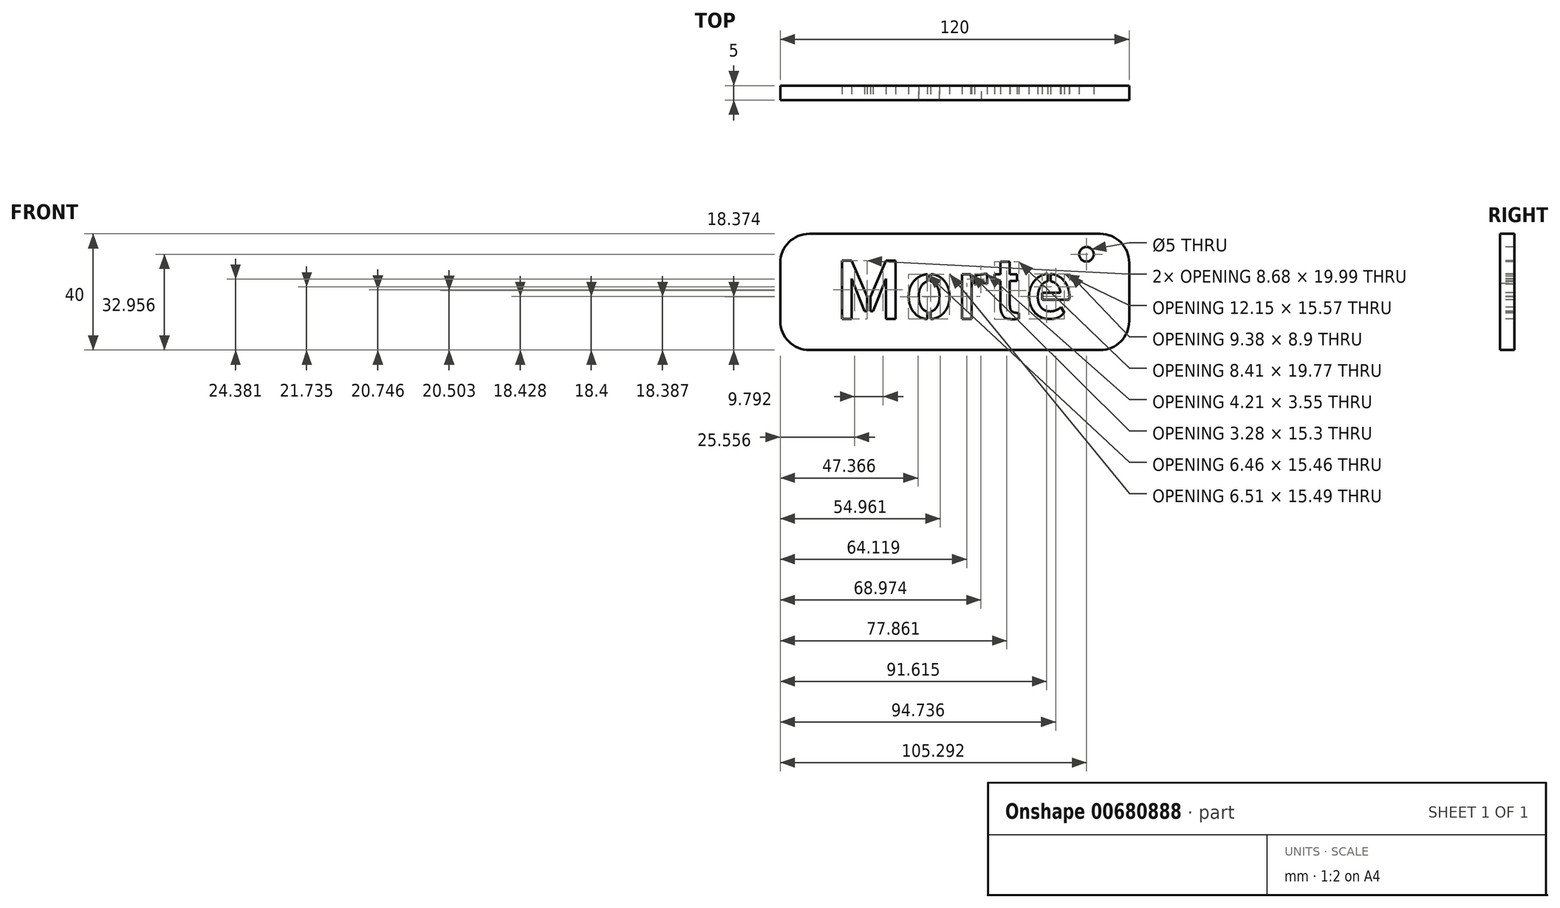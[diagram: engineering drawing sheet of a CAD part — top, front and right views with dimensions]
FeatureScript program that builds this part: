
annotation { "Feature Type Name" : "Feature", "Feature Type Description" : "" }
export const myFeature = defineFeature(function(context is Context, id is Id, definition is map)
    precondition{}
    {
        {
            var Q0;
            Q0=qCreatedBy(makeId("Front.planeOp"),FACE);
            var sketch = newSketch(context, id + "F0", { "sketchPlane" : qUnion([Q0])});
            skLineSegment(sketch, "E0.bottom", {"start": v(0, 0) * mm, "end": v(120, 0) * mm});
            skLineSegment(sketch, "E0.top", {"start": v(0, 40) * mm, "end": v(120, 40) * mm});
            skLineSegment(sketch, "E0.left", {"start": v(0, 0) * mm, "end": v(0, 40) * mm});
            skLineSegment(sketch, "E0.right", {"start": v(120, 0) * mm, "end": v(120, 40) * mm});
            skPoint(sketch, "E1", {"position": v(0, 20) * mm});
            skPoint(sketch, "E2", {"position": v(60, 40) * mm});
            skText(sketch, "E3", { "text": "Morte", "fontName": "AllertaStencil-Regular.ttf"});
            skPoint(sketch, "E4", {"position": v(18.72, 20.75) * mm});
            const initialGuessF0  = {"E3": [0.01872, 0.01075, 1, 0, 0.02]};
            skSetInitialGuess(sketch, initialGuessF0);
            skSolve(sketch);
        }
        {
            var Q0;
            Q0 = qSketchRegion(id + "F0", true);
            var Q1;
            Q1=makeQuery(id+"F0.imprint","IMPRINT",FACE,{"disambiguationData":[TD([[makeQuery(id+"F0.imprint","IMPRINT",EDGE,{"derivedFrom":sQuery(id+"F0.wireOp",EDGE,"E3.sketch_text.stroke-27")}),1.0]])]});
            var Q2;
            Q2=makeQuery(id+"F0.imprint","IMPRINT",FACE,{"disambiguationData":[TD([[makeQuery(id+"F0.imprint","IMPRINT",EDGE,{"derivedFrom":sQuery(id+"F0.wireOp",EDGE,"E3.sketch_text.stroke-81")}),1.0]])]});
            extrude(context, id + "F1", {"entities" : qUnion([Q0, Q1, Q2]), "oppositeDirection" : true, "depth" : 5 * mm, "offsetDistance" : 25 * mm});
        }
        {
            var Q0;
            Q0=makeQuery(id+"F1.opExtrude","SWEPT_EDGE",EDGE,{"disambiguationData":[OSD([sQuery(id+"F0.wireOp",EDGE,"E0.top"),sQuery(id+"F0.wireOp",EDGE,"E0.left")])]});
            var Q1;
            Q1=makeQuery(id+"F1.opExtrude","SWEPT_EDGE",EDGE,{"disambiguationData":[OSD([sQuery(id+"F0.wireOp",EDGE,"E0.bottom"),sQuery(id+"F0.wireOp",EDGE,"E0.left")])]});
            var Q2;
            Q2=makeQuery(id+"F1.opExtrude","SWEPT_EDGE",EDGE,{"disambiguationData":[OSD([sQuery(id+"F0.wireOp",EDGE,"E0.top"),sQuery(id+"F0.wireOp",EDGE,"E0.right")])]});
            var Q3;
            Q3=makeQuery(id+"F1.opExtrude","SWEPT_EDGE",EDGE,{"disambiguationData":[OSD([sQuery(id+"F0.wireOp",EDGE,"E0.bottom"),sQuery(id+"F0.wireOp",EDGE,"E0.right")])]});
            fillet(context, id + "F2", {"entities" : qUnion([Q0, Q1, Q2, Q3]), "radius" : 10 * mm, "tangentPropagation" : true, "allowEdgeOverflow" : false});
        }
        {
            var Q0;
            Q0=makeQuery(id+"F1.opExtrude","CAP_FACE",FACE,{"disambiguationData":[OSD([sQuery(id+"F0.wireOp",EDGE,"E0.bottom"),sQuery(id+"F0.wireOp",EDGE,"E0.top"),sQuery(id+"F0.wireOp",EDGE,"E0.left"),sQuery(id+"F0.wireOp",EDGE,"E0.right"),sQuery(id+"F0.wireOp",EDGE,"E3.sketch_text.stroke-0"),sQuery(id+"F0.wireOp",EDGE,"E3.sketch_text.stroke-1"),sQuery(id+"F0.wireOp",EDGE,"E3.sketch_text.stroke-2"),sQuery(id+"F0.wireOp",EDGE,"E3.sketch_text.stroke-3"),sQuery(id+"F0.wireOp",EDGE,"E3.sketch_text.stroke-4"),sQuery(id+"F0.wireOp",EDGE,"E3.sketch_text.stroke-5"),sQuery(id+"F0.wireOp",EDGE,"E3.sketch_text.stroke-6"),sQuery(id+"F0.wireOp",EDGE,"E3.sketch_text.stroke-7"),sQuery(id+"F0.wireOp",EDGE,"E3.sketch_text.stroke-8"),sQuery(id+"F0.wireOp",EDGE,"E3.sketch_text.stroke-9"),sQuery(id+"F0.wireOp",EDGE,"E3.sketch_text.stroke-10"),sQuery(id+"F0.wireOp",EDGE,"E3.sketch_text.stroke-11"),sQuery(id+"F0.wireOp",EDGE,"E3.sketch_text.stroke-12"),sQuery(id+"F0.wireOp",EDGE,"E3.sketch_text.stroke-13"),sQuery(id+"F0.wireOp",EDGE,"E3.sketch_text.stroke-14"),sQuery(id+"F0.wireOp",EDGE,"E3.sketch_text.stroke-15"),sQuery(id+"F0.wireOp",EDGE,"E3.sketch_text.stroke-16"),sQuery(id+"F0.wireOp",EDGE,"E3.sketch_text.stroke-17"),sQuery(id+"F0.wireOp",EDGE,"E3.sketch_text.stroke-18"),sQuery(id+"F0.wireOp",EDGE,"E3.sketch_text.stroke-19"),sQuery(id+"F0.wireOp",EDGE,"E3.sketch_text.stroke-20"),sQuery(id+"F0.wireOp",EDGE,"E3.sketch_text.stroke-21"),sQuery(id+"F0.wireOp",EDGE,"E3.sketch_text.stroke-22"),sQuery(id+"F0.wireOp",EDGE,"E3.sketch_text.stroke-23"),sQuery(id+"F0.wireOp",EDGE,"E3.sketch_text.stroke-24"),sQuery(id+"F0.wireOp",EDGE,"E3.sketch_text.stroke-25"),sQuery(id+"F0.wireOp",EDGE,"E3.sketch_text.stroke-26"),sQuery(id+"F0.wireOp",EDGE,"E3.sketch_text.stroke-27"),sQuery(id+"F0.wireOp",EDGE,"E3.sketch_text.stroke-28"),sQuery(id+"F0.wireOp",EDGE,"E3.sketch_text.stroke-29"),sQuery(id+"F0.wireOp",EDGE,"E3.sketch_text.stroke-30"),sQuery(id+"F0.wireOp",EDGE,"E3.sketch_text.stroke-31"),sQuery(id+"F0.wireOp",EDGE,"E3.sketch_text.stroke-32"),sQuery(id+"F0.wireOp",EDGE,"E3.sketch_text.stroke-33"),sQuery(id+"F0.wireOp",EDGE,"E3.sketch_text.stroke-34"),sQuery(id+"F0.wireOp",EDGE,"E3.sketch_text.stroke-35"),sQuery(id+"F0.wireOp",EDGE,"E3.sketch_text.stroke-36"),sQuery(id+"F0.wireOp",EDGE,"E3.sketch_text.stroke-37"),sQuery(id+"F0.wireOp",EDGE,"E3.sketch_text.stroke-38"),sQuery(id+"F0.wireOp",EDGE,"E3.sketch_text.stroke-39"),sQuery(id+"F0.wireOp",EDGE,"E3.sketch_text.stroke-40"),sQuery(id+"F0.wireOp",EDGE,"E3.sketch_text.stroke-41"),sQuery(id+"F0.wireOp",EDGE,"E3.sketch_text.stroke-42"),sQuery(id+"F0.wireOp",EDGE,"E3.sketch_text.stroke-43"),sQuery(id+"F0.wireOp",EDGE,"E3.sketch_text.stroke-44"),sQuery(id+"F0.wireOp",EDGE,"E3.sketch_text.stroke-45"),sQuery(id+"F0.wireOp",EDGE,"E3.sketch_text.stroke-46"),sQuery(id+"F0.wireOp",EDGE,"E3.sketch_text.stroke-47"),sQuery(id+"F0.wireOp",EDGE,"E3.sketch_text.stroke-48"),sQuery(id+"F0.wireOp",EDGE,"E3.sketch_text.stroke-49"),sQuery(id+"F0.wireOp",EDGE,"E3.sketch_text.stroke-50"),sQuery(id+"F0.wireOp",EDGE,"E3.sketch_text.stroke-51"),sQuery(id+"F0.wireOp",EDGE,"E3.sketch_text.stroke-52"),sQuery(id+"F0.wireOp",EDGE,"E3.sketch_text.stroke-53"),sQuery(id+"F0.wireOp",EDGE,"E3.sketch_text.stroke-54"),sQuery(id+"F0.wireOp",EDGE,"E3.sketch_text.stroke-55"),sQuery(id+"F0.wireOp",EDGE,"E3.sketch_text.stroke-56"),sQuery(id+"F0.wireOp",EDGE,"E3.sketch_text.stroke-57"),sQuery(id+"F0.wireOp",EDGE,"E3.sketch_text.stroke-58"),sQuery(id+"F0.wireOp",EDGE,"E3.sketch_text.stroke-59"),sQuery(id+"F0.wireOp",EDGE,"E3.sketch_text.stroke-60"),sQuery(id+"F0.wireOp",EDGE,"E3.sketch_text.stroke-61"),sQuery(id+"F0.wireOp",EDGE,"E3.sketch_text.stroke-62"),sQuery(id+"F0.wireOp",EDGE,"E3.sketch_text.stroke-63"),sQuery(id+"F0.wireOp",EDGE,"E3.sketch_text.stroke-64"),sQuery(id+"F0.wireOp",EDGE,"E3.sketch_text.stroke-65"),sQuery(id+"F0.wireOp",EDGE,"E3.sketch_text.stroke-66"),sQuery(id+"F0.wireOp",EDGE,"E3.sketch_text.stroke-67"),sQuery(id+"F0.wireOp",EDGE,"E3.sketch_text.stroke-68"),sQuery(id+"F0.wireOp",EDGE,"E3.sketch_text.stroke-69"),sQuery(id+"F0.wireOp",EDGE,"E3.sketch_text.stroke-70"),sQuery(id+"F0.wireOp",EDGE,"E3.sketch_text.stroke-71"),sQuery(id+"F0.wireOp",EDGE,"E3.sketch_text.stroke-72"),sQuery(id+"F0.wireOp",EDGE,"E3.sketch_text.stroke-73"),sQuery(id+"F0.wireOp",EDGE,"E3.sketch_text.stroke-74"),sQuery(id+"F0.wireOp",EDGE,"E3.sketch_text.stroke-75"),sQuery(id+"F0.wireOp",EDGE,"E3.sketch_text.stroke-76"),sQuery(id+"F0.wireOp",EDGE,"E3.sketch_text.stroke-77"),sQuery(id+"F0.wireOp",EDGE,"E3.sketch_text.stroke-78"),sQuery(id+"F0.wireOp",EDGE,"E3.sketch_text.stroke-79"),sQuery(id+"F0.wireOp",EDGE,"E3.sketch_text.stroke-80"),sQuery(id+"F0.wireOp",EDGE,"E3.sketch_text.stroke-81"),sQuery(id+"F0.wireOp",EDGE,"E3.sketch_text.stroke-82"),sQuery(id+"F0.wireOp",EDGE,"E3.sketch_text.stroke-83"),sQuery(id+"F0.wireOp",EDGE,"E3.sketch_text.stroke-84"),sQuery(id+"F0.wireOp",EDGE,"E3.sketch_text.stroke-85"),sQuery(id+"F0.wireOp",EDGE,"E3.sketch_text.stroke-86"),sQuery(id+"F0.wireOp",EDGE,"E3.sketch_text.stroke-87"),sQuery(id+"F0.wireOp",EDGE,"E3.sketch_text.stroke-88"),sQuery(id+"F0.wireOp",EDGE,"E3.sketch_text.stroke-89"),sQuery(id+"F0.wireOp",EDGE,"E3.sketch_text.stroke-90"),sQuery(id+"F0.wireOp",EDGE,"E3.sketch_text.stroke-91"),sQuery(id+"F0.wireOp",EDGE,"E3.sketch_text.stroke-92"),sQuery(id+"F0.wireOp",EDGE,"E3.sketch_text.stroke-93"),sQuery(id+"F0.wireOp",EDGE,"E3.sketch_text.stroke-94"),sQuery(id+"F0.wireOp",EDGE,"E3.sketch_text.stroke-95"),sQuery(id+"F0.wireOp",EDGE,"E3.sketch_text.stroke-96"),sQuery(id+"F0.wireOp",EDGE,"E3.sketch_text.stroke-97"),sQuery(id+"F0.wireOp",EDGE,"E3.sketch_text.stroke-98"),sQuery(id+"F0.wireOp",EDGE,"E3.sketch_text.stroke-99"),sQuery(id+"F0.wireOp",EDGE,"E3.sketch_text.stroke-100"),sQuery(id+"F0.wireOp",EDGE,"E3.sketch_text.stroke-101"),sQuery(id+"F0.wireOp",EDGE,"E3.sketch_text.stroke-102"),sQuery(id+"F0.wireOp",EDGE,"E3.sketch_text.stroke-103"),sQuery(id+"F0.wireOp",EDGE,"E3.sketch_text.stroke-104"),sQuery(id+"F0.wireOp",EDGE,"E3.sketch_text.stroke-105"),sQuery(id+"F0.wireOp",EDGE,"E3.sketch_text.stroke-106"),sQuery(id+"F0.wireOp",EDGE,"E3.sketch_text.stroke-107"),sQuery(id+"F0.wireOp",EDGE,"E3.sketch_text.stroke-108"),sQuery(id+"F0.wireOp",EDGE,"E3.sketch_text.stroke-109"),sQuery(id+"F0.wireOp",EDGE,"E3.sketch_text.stroke-110"),sQuery(id+"F0.wireOp",EDGE,"E3.sketch_text.stroke-111"),sQuery(id+"F0.wireOp",EDGE,"E3.sketch_text.stroke-112"),sQuery(id+"F0.wireOp",EDGE,"E3.sketch_text.stroke-113"),sQuery(id+"F0.wireOp",EDGE,"E3.sketch_text.stroke-114"),sQuery(id+"F0.wireOp",EDGE,"E3.sketch_text.stroke-115"),sQuery(id+"F0.wireOp",EDGE,"E3.sketch_text.stroke-116"),sQuery(id+"F0.wireOp",EDGE,"E3.sketch_text.stroke-117"),sQuery(id+"F0.wireOp",EDGE,"E3.sketch_text.stroke-118"),sQuery(id+"F0.wireOp",EDGE,"E3.sketch_text.stroke-119"),sQuery(id+"F0.wireOp",EDGE,"E3.sketch_text.stroke-120"),sQuery(id+"F0.wireOp",EDGE,"E3.sketch_text.stroke-121"),sQuery(id+"F0.wireOp",EDGE,"E3.sketch_text.stroke-122"),sQuery(id+"F0.wireOp",EDGE,"E3.sketch_text.stroke-123")])],"isStart":true});
            var sketch = newSketch(context, id + "F3", { "sketchPlane" : qUnion([Q0])});
            skCircle(sketch, "E5", {"center": v(105.3, 32.96) * mm, "radius": 2.5 * mm});
            skSolve(sketch);
        }
        {
            var Q0;
            Q0 = qSketchRegion(id + "F3", true);
            extrude(context, id + "F4", {"entities" : qUnion([Q0]), "operationType" : NewBodyOperationType.REMOVE, "oppositeDirection" : true, "depth" : 25 * mm, "offsetDistance" : 25 * mm});
        }
    });
